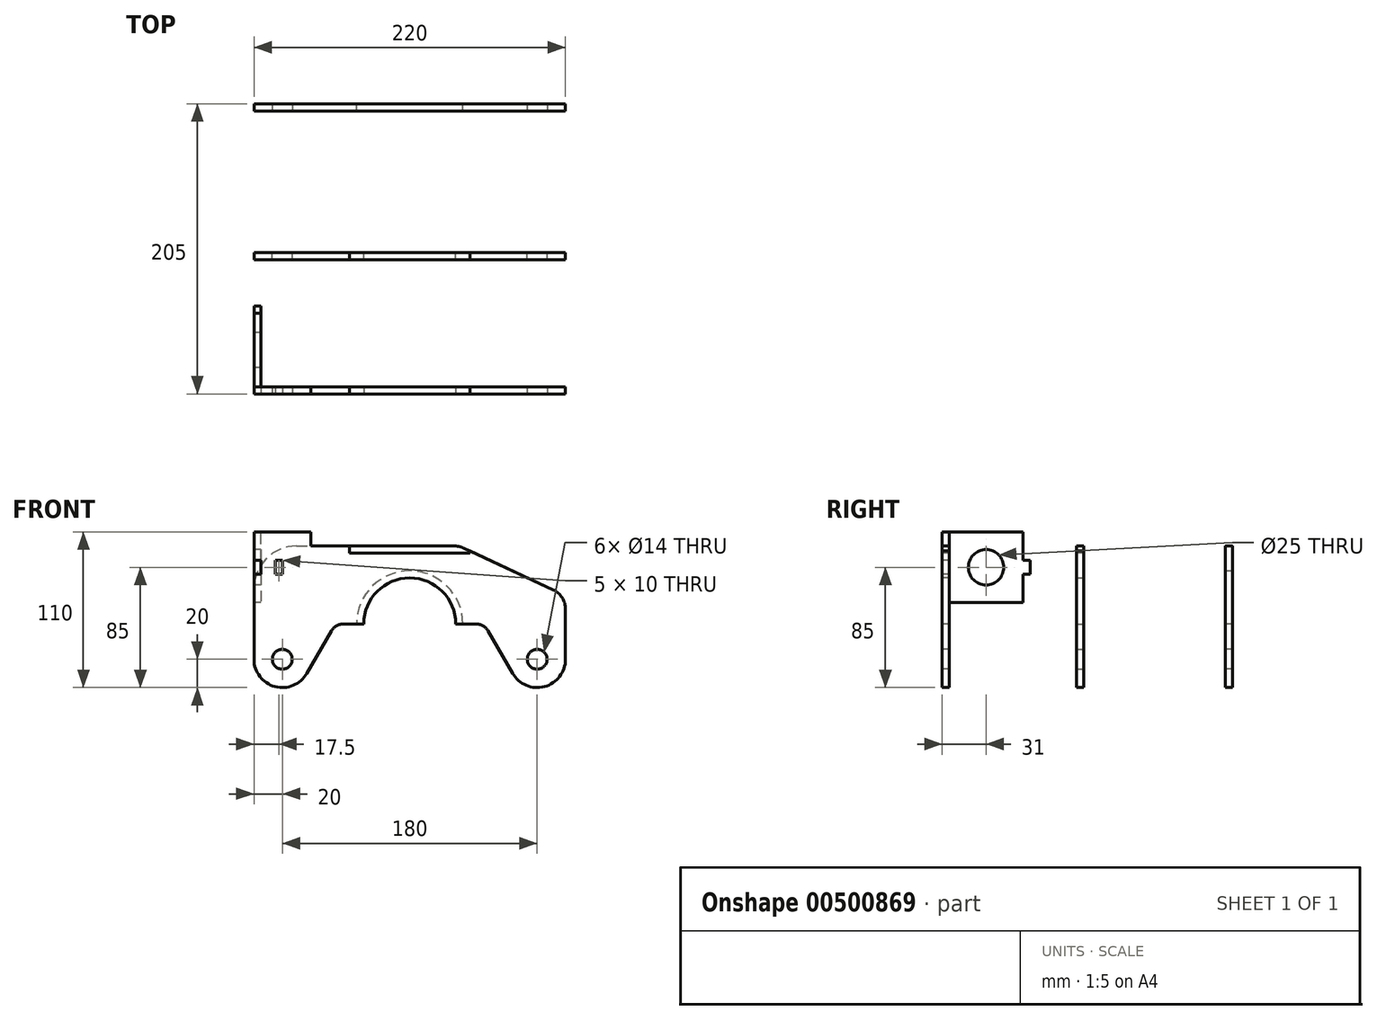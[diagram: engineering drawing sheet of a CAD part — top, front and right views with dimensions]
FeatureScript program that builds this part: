
annotation { "Feature Type Name" : "Feature", "Feature Type Description" : "" }
export const myFeature = defineFeature(function(context is Context, id is Id, definition is map)
    precondition{}
    {
        {
            var Q0;
            Q0=qCreatedBy(makeId("Front.planeOp"),FACE);
            var sketch = newSketch(context, id + "F0", { "sketchPlane" : qUnion([Q0])});
            skArc(sketch, "E0", {"start": v(32.5, 0) * mm, "mid": v(0, 32.5) * mm, "end": v(-32.5, 0) * mm});
            skLineSegment(sketch, "E1", {"start": v(-32.5, 0) * mm, "end": v(32.5, 0) * mm, "construction": true});
            skPoint(sketch, "E2", {"position": v(-90, -25) * mm});
            skCircle(sketch, "E3", {"center": v(-90, -25) * mm, "radius": 7 * mm});
            skCircle(sketch, "E4", {"center": v(-90, -25) * mm, "radius": 20 * mm});
            skPoint(sketch, "E5", {"position": v(90, -25) * mm});
            skCircle(sketch, "E6", {"center": v(90, -25) * mm, "radius": 7 * mm});
            skCircle(sketch, "E7", {"center": v(90, -25) * mm, "radius": 20 * mm});
            skPoint(sketch, "E8", {"position": v(-110, -25) * mm});
            skPoint(sketch, "E9", {"position": v(110, -25) * mm});
            skLineSegment(sketch, "E10", {"start": v(-110, -25) * mm, "end": v(-110, 25) * mm});
            skLineSegment(sketch, "E11", {"start": v(-80, 55) * mm, "end": v(110, 55) * mm});
            skLineSegment(sketch, "E12", {"start": v(110, 55) * mm, "end": v(110, -25) * mm});
            skLineSegment(sketch, "E13", {"start": v(-32.5, 0) * mm, "end": v(-46.72, 0) * mm});
            skLineSegment(sketch, "E14", {"start": v(32.5, 0) * mm, "end": v(46.72, 0) * mm});
            skLineSegment(sketch, "E15", {"start": v(-55.39, -5) * mm, "end": v(-72.67, -34.99) * mm});
            skLineSegment(sketch, "E16", {"start": v(55.39, -5) * mm, "end": v(72.67, -34.99) * mm});
            skPoint(sketch, "E17.visualSharp", {"position": v(-52.5, 0) * mm});
            skArc(sketch, "E17.filletArc", {"start": v(-46.72, 0) * mm, "mid": v(-51.73, -1.34) * mm, "end": v(-55.39, -5) * mm});
            skPoint(sketch, "E18.visualSharp", {"position": v(52.5, 0) * mm});
            skArc(sketch, "E18.filletArc", {"start": v(55.39, -5) * mm, "mid": v(51.73, -1.34) * mm, "end": v(46.72, 0) * mm});
            skPoint(sketch, "E19.visualSharp", {"position": v(-110, 55) * mm});
            skArc(sketch, "E19.filletArc", {"start": v(-80, 55) * mm, "mid": v(-101.21, 46.21) * mm, "end": v(-110, 25) * mm});
            skPoint(sketch, "E20.visualSharp", {"position": v(110, 55) * mm});
            skLineSegment(sketch, "E20.filletArc", {"start": v(110, 55) * mm, "end": v(110, 55) * mm});
            skPoint(sketch, "E21", {"position": v(110, 20) * mm});
            skPoint(sketch, "E22", {"position": v(35, 55) * mm});
            skLineSegment(sketch, "E23", {"start": v(35, 55) * mm, "end": v(110, 20) * mm});
            skSolve(sketch);
        }
        {
            var Q0;
            Q0=makeQuery(id+"F0.imprint","IMPRINT",FACE,{"disambiguationData":[TD([[makeQuery(id+"F0.imprint","IMPRINT",EDGE,{"derivedFrom":sQuery(id+"F0.wireOp",EDGE,"E3")}),-1.0]])]});
            var Q1;
            Q1=makeQuery(id+"F0.imprint","IMPRINT",FACE,{"disambiguationData":[TD([[makeQuery(id+"F0.imprint","IMPRINT",EDGE,{"derivedFrom":sQuery(id+"F0.wireOp",EDGE,"E6")}),-1.0]])]});
            var Q2;
            Q2=makeQuery(id+"F0.imprint","IMPRINT",FACE,{"disambiguationData":[TD([[makeQuery(id+"F0.imprint","IMPRINT",EDGE,{"derivedFrom":sQuery(id+"F0.wireOp",EDGE,"E0")}),-1.0]])]});
            extrude(context, id + "F1", {"entities" : qUnion([Q0, Q1, Q2]), "depth" : 5 * mm, "offsetDistance" : 25 * mm});
        }
        {
            var Q0;
            Q0=qCreatedBy(makeId("Front.planeOp"),FACE);
            cPlane(context, id + "F2", {"entities" : qUnion([Q0]), "cplaneType" : CPlaneType.OFFSET, "offset" : 50 * mm, "oppositeDirection" : true, "width" : 150 * mm, "height" : 150 * mm});
        }
        {
            var Q0;
            Q0=makeQuery(id+"F1.opExtrude","SWEPT_BODY",BODY,{"disambiguationData":[OSD([sQuery(id+"F0.wireOp",EDGE,"E0"),sQuery(id+"F0.wireOp",EDGE,"wYGwPTdj-hQ3h-UPXI-DBvO-CMdxX0ZBpIs3"),sQuery(id+"F0.wireOp",EDGE,"x7k1yNY0-FdVM-nHSz-DSX0-2XPxu6rrP0qx"),sQuery(id+"F0.wireOp",EDGE,"9FEWUdX1-vxY7-CqPM-wlNF-PPAwq3WJZH4g"),sQuery(id+"F0.wireOp",EDGE,"gDaBEeFt-Z0H3-VczB-V8Bx-S3RSHxuVBjjS"),sQuery(id+"F0.wireOp",EDGE,"murKOrwq-gOHJ-bXzC-ZGz9-tcrJ8arLhTBh"),sQuery(id+"F0.wireOp",EDGE,"XS1oxogV-xBYE-ZJ7y-Qyi2-3TEannQxHCB3"),sQuery(id+"F0.wireOp",EDGE,"UnKacQbt-6CPZ-4kxL-4eNt-IC4GjbSk1ORf"),sQuery(id+"F0.wireOp",EDGE,"afb97e3d-8f33-4936-9a61-d90580ab6d3b.filletArc"),sQuery(id+"F0.wireOp",EDGE,"c8fba1ef-1978-42b1-8804-f232b3c369ea.filletArc"),sQuery(id+"F0.wireOp",EDGE,"X5k6Ah4p-kY58-pmaY-KI1E-PuHpooEfadsh"),sQuery(id+"F0.wireOp",EDGE,"EwHy3WlO-al0v-v5lV-Htfk-dZK2AdyTbM4l"),sQuery(id+"F0.wireOp",EDGE,"sK6yQUJL-bbSg-vOET-FAIG-DtKAZYSsNfgG"),sQuery(id+"F0.wireOp",EDGE,"gzghe2TM-HSCt-wxjk-NPDM-RHRqv8zNIVQs"),sQuery(id+"F0.wireOp",EDGE,"0c25a0b1-6eda-4544-9dcf-9f9016e37f78.filletArc"),sQuery(id+"F0.wireOp",EDGE,"3fe3a689-dd35-411c-a34f-f7a2c4317feb.filletArc")])]});
            var Q1;
            Q1=qCreatedBy(id+"F2.planeOp",FACE);
            mirror(context, id + "F3", {"entities" : qUnion([Q0]), "mirrorPlane" : qUnion([Q1])});
        }
        {
            var Q0;
            Q0=makeQuery(id+"F3.opPattern","COPY",FACE,{"derivedFrom":makeQuery(id+"F1.opExtrude","CAP_FACE",FACE,{"disambiguationData":[OSD([sQuery(id+"F0.wireOp",EDGE,"E0"),sQuery(id+"F0.wireOp",EDGE,"wYGwPTdj-hQ3h-UPXI-DBvO-CMdxX0ZBpIs3"),sQuery(id+"F0.wireOp",EDGE,"x7k1yNY0-FdVM-nHSz-DSX0-2XPxu6rrP0qx"),sQuery(id+"F0.wireOp",EDGE,"9FEWUdX1-vxY7-CqPM-wlNF-PPAwq3WJZH4g"),sQuery(id+"F0.wireOp",EDGE,"gDaBEeFt-Z0H3-VczB-V8Bx-S3RSHxuVBjjS"),sQuery(id+"F0.wireOp",EDGE,"murKOrwq-gOHJ-bXzC-ZGz9-tcrJ8arLhTBh"),sQuery(id+"F0.wireOp",EDGE,"XS1oxogV-xBYE-ZJ7y-Qyi2-3TEannQxHCB3"),sQuery(id+"F0.wireOp",EDGE,"UnKacQbt-6CPZ-4kxL-4eNt-IC4GjbSk1ORf"),sQuery(id+"F0.wireOp",EDGE,"afb97e3d-8f33-4936-9a61-d90580ab6d3b.filletArc"),sQuery(id+"F0.wireOp",EDGE,"c8fba1ef-1978-42b1-8804-f232b3c369ea.filletArc"),sQuery(id+"F0.wireOp",EDGE,"X5k6Ah4p-kY58-pmaY-KI1E-PuHpooEfadsh"),sQuery(id+"F0.wireOp",EDGE,"EwHy3WlO-al0v-v5lV-Htfk-dZK2AdyTbM4l"),sQuery(id+"F0.wireOp",EDGE,"sK6yQUJL-bbSg-vOET-FAIG-DtKAZYSsNfgG"),sQuery(id+"F0.wireOp",EDGE,"gzghe2TM-HSCt-wxjk-NPDM-RHRqv8zNIVQs"),sQuery(id+"F0.wireOp",EDGE,"0c25a0b1-6eda-4544-9dcf-9f9016e37f78.filletArc"),sQuery(id+"F0.wireOp",EDGE,"3fe3a689-dd35-411c-a34f-f7a2c4317feb.filletArc")])],"isStart":false}),"instanceName":"1"});
            var sketch = newSketch(context, id + "F4", { "sketchPlane" : qUnion([Q0])});
            skLineSegment(sketch, "E24.0", {"start": v(-32.5, 0) * mm, "end": v(-32.5, 0) * mm});
            skCircle(sketch, "E25", {"center": v(0, 0) * mm, "radius": 37.5 * mm});
            skLineSegment(sketch, "E26", {"start": v(0, 0) * mm, "end": v(37.5, 0) * mm});
            skSolve(sketch);
        }
        {
            var Q0;
            Q0 = qSketchRegion(id + "F4", true);
            extrude(context, id + "F5", {"entities" : qUnion([Q0]), "operationType" : NewBodyOperationType.REMOVE, "oppositeDirection" : true, "depth" : 25 * mm, "offsetDistance" : 25 * mm});
        }
        {
            var Q0;
            Q0=qCreatedBy(makeId("Front.planeOp"),FACE);
            cPlane(context, id + "F6", {"entities" : qUnion([Q0]), "cplaneType" : CPlaneType.OFFSET, "offset" : 50 * mm, "width" : 150 * mm, "height" : 150 * mm});
        }
        {
            var Q0;
            Q0=makeQuery(id+"F1.opExtrude","SWEPT_BODY",BODY,{"disambiguationData":[OSD([sQuery(id+"F0.wireOp",EDGE,"E0"),sQuery(id+"F0.wireOp",EDGE,"wYGwPTdj-hQ3h-UPXI-DBvO-CMdxX0ZBpIs3"),sQuery(id+"F0.wireOp",EDGE,"x7k1yNY0-FdVM-nHSz-DSX0-2XPxu6rrP0qx"),sQuery(id+"F0.wireOp",EDGE,"9FEWUdX1-vxY7-CqPM-wlNF-PPAwq3WJZH4g"),sQuery(id+"F0.wireOp",EDGE,"gDaBEeFt-Z0H3-VczB-V8Bx-S3RSHxuVBjjS"),sQuery(id+"F0.wireOp",EDGE,"murKOrwq-gOHJ-bXzC-ZGz9-tcrJ8arLhTBh"),sQuery(id+"F0.wireOp",EDGE,"XS1oxogV-xBYE-ZJ7y-Qyi2-3TEannQxHCB3"),sQuery(id+"F0.wireOp",EDGE,"UnKacQbt-6CPZ-4kxL-4eNt-IC4GjbSk1ORf"),sQuery(id+"F0.wireOp",EDGE,"afb97e3d-8f33-4936-9a61-d90580ab6d3b.filletArc"),sQuery(id+"F0.wireOp",EDGE,"c8fba1ef-1978-42b1-8804-f232b3c369ea.filletArc"),sQuery(id+"F0.wireOp",EDGE,"X5k6Ah4p-kY58-pmaY-KI1E-PuHpooEfadsh"),sQuery(id+"F0.wireOp",EDGE,"EwHy3WlO-al0v-v5lV-Htfk-dZK2AdyTbM4l"),sQuery(id+"F0.wireOp",EDGE,"sK6yQUJL-bbSg-vOET-FAIG-DtKAZYSsNfgG"),sQuery(id+"F0.wireOp",EDGE,"gzghe2TM-HSCt-wxjk-NPDM-RHRqv8zNIVQs"),sQuery(id+"F0.wireOp",EDGE,"0c25a0b1-6eda-4544-9dcf-9f9016e37f78.filletArc"),sQuery(id+"F0.wireOp",EDGE,"3fe3a689-dd35-411c-a34f-f7a2c4317feb.filletArc")])]});
            var Q1;
            Q1=qCreatedBy(id+"F6.planeOp",FACE);
            mirror(context, id + "F7", {"entities" : qUnion([Q0]), "mirrorPlane" : qUnion([Q1])});
        }
        {
            var Q0;
            Q0=makeQuery(id+"F7.opPattern","COPY",FACE,{"derivedFrom":makeQuery(id+"F1.opExtrude","CAP_FACE",FACE,{"disambiguationData":[OSD([sQuery(id+"F0.wireOp",EDGE,"E0"),sQuery(id+"F0.wireOp",EDGE,"E3"),sQuery(id+"F0.wireOp",EDGE,"E4"),sQuery(id+"F0.wireOp",EDGE,"E6"),sQuery(id+"F0.wireOp",EDGE,"E7"),sQuery(id+"F0.wireOp",EDGE,"E10"),sQuery(id+"F0.wireOp",EDGE,"E11"),sQuery(id+"F0.wireOp",EDGE,"E12"),sQuery(id+"F0.wireOp",EDGE,"E13"),sQuery(id+"F0.wireOp",EDGE,"E14"),sQuery(id+"F0.wireOp",EDGE,"E15"),sQuery(id+"F0.wireOp",EDGE,"E16"),sQuery(id+"F0.wireOp",EDGE,"E17.filletArc"),sQuery(id+"F0.wireOp",EDGE,"E18.filletArc"),sQuery(id+"F0.wireOp",EDGE,"E19.filletArc"),sQuery(id+"F0.wireOp",EDGE,"E20.filletArc")])],"isStart":true}),"instanceName":"1"});
            var sketch = newSketch(context, id + "F8", { "sketchPlane" : qUnion([Q0])});
            skLineSegment(sketch, "E27.0", {"start": v(-110, -25) * mm, "end": v(-110, 25) * mm});
            skLineSegment(sketch, "E28.0", {"start": v(-80, 55) * mm, "end": v(-80, 55) * mm});
            skLineSegment(sketch, "E29", {"start": v(-110, 55) * mm, "end": v(-110, 65) * mm});
            skLineSegment(sketch, "E30", {"start": v(-110, 55) * mm, "end": v(-110, 25) * mm});
            skLineSegment(sketch, "E31", {"start": v(-110, 65) * mm, "end": v(-70, 65) * mm});
            skLineSegment(sketch, "E32", {"start": v(-70, 65) * mm, "end": v(-70, 55) * mm});
            skPoint(sketch, "E33", {"position": v(-110, 45) * mm});
            skLineSegment(sketch, "E34.bottom", {"start": v(-110, 45) * mm, "end": v(-105, 45) * mm});
            skLineSegment(sketch, "E34.top", {"start": v(-110, 35) * mm, "end": v(-105, 35) * mm});
            skLineSegment(sketch, "E34.left", {"start": v(-110, 45) * mm, "end": v(-110, 35) * mm});
            skLineSegment(sketch, "E34.right", {"start": v(-105, 45) * mm, "end": v(-105, 35) * mm});
            skLineSegment(sketch, "E35.bottom", {"start": v(-95, 45) * mm, "end": v(-90, 45) * mm});
            skLineSegment(sketch, "E35.top", {"start": v(-95, 35) * mm, "end": v(-90, 35) * mm});
            skLineSegment(sketch, "E35.left", {"start": v(-95, 45) * mm, "end": v(-95, 35) * mm});
            skLineSegment(sketch, "E35.right", {"start": v(-90, 45) * mm, "end": v(-90, 35) * mm});
            skArc(sketch, "E36.0", {"start": v(-80, 55) * mm, "mid": v(-101.21, 46.21) * mm, "end": v(-110, 25) * mm});
            skSolve(sketch);
        }
        {
            var Q0;
            {var subQ1=sQuery(id+"F8.wireOp",EDGE,"E29");Q0=makeQuery(id+"F8.imprint","IMPRINT",FACE,{"disambiguationData":[TD([[makeQuery(id+"F8.imprint","IMPRINT",EDGE,{"derivedFrom":subQ1}),-1.0]])]});}
            var Q1;
            {var subQ1=sQuery(id+"F8.wireOp",EDGE,"E34.bottom");Q1=makeQuery(id+"F8.imprint","IMPRINT",FACE,{"disambiguationData":[TD([[makeQuery(id+"F8.imprint","IMPRINT",EDGE,{"derivedFrom":subQ1}),-1.0]])]});}
            var Q2;
            {var subQ0=sQuery(id+"F8.wireOp",EDGE,"E36.0");var subQ3=sQuery(id+"F8.wireOp",EDGE,"E34.top");var subQ5=makeQuery(id+"F8.imprint","INTERSECT",VERTEX,{"derivedFrom":[subQ3,subQ0]});Q2=makeQuery(id+"F8.imprint","IMPRINT",FACE,{"disambiguationData":[TD([[makeQuery(id+"F8.imprint","IMPRINT",EDGE,{"disambiguationData":[TD([[subQ5,1.0]])],"derivedFrom":subQ3}),-1.0]])]});}
            extrude(context, id + "F9", {"entities" : qUnion([Q0, Q1, Q2]), "operationType" : NewBodyOperationType.ADD, "oppositeDirection" : true, "depth" : 5 * mm, "offsetDistance" : 25 * mm});
        }
        {
            var Q0;
            Q0=makeQuery(id+"F8.imprint","IMPRINT",FACE,{"disambiguationData":[TD([[makeQuery(id+"F8.imprint","IMPRINT",EDGE,{"derivedFrom":sQuery(id+"F8.wireOp",EDGE,"E35.bottom")}),-1.0]])]});
            var Q1;
            {var subQ1=sQuery(id+"F8.wireOp",EDGE,"E34.bottom");Q1=makeQuery(id+"F8.imprint","IMPRINT",FACE,{"disambiguationData":[TD([[makeQuery(id+"F8.imprint","IMPRINT",EDGE,{"derivedFrom":subQ1}),-1.0]])]});}
            var Q2;
            {var subQ0=sQuery(id+"F8.wireOp",EDGE,"E34.right");var subQ1=sQuery(id+"F8.wireOp",EDGE,"E34.top");var subQ2=makeQuery(id+"F8.imprint","INTERSECT",VERTEX,{"derivedFrom":[subQ1,subQ0]});Q2=makeQuery(id+"F8.imprint","IMPRINT",FACE,{"disambiguationData":[TD([[makeQuery(id+"F8.imprint","IMPRINT",EDGE,{"disambiguationData":[TD([[subQ2,1.0]])],"derivedFrom":subQ1}),1.0]])]});}
            extrude(context, id + "F10", {"entities" : qUnion([Q0, Q1, Q2]), "operationType" : NewBodyOperationType.REMOVE, "oppositeDirection" : true, "depth" : 25 * mm, "offsetDistance" : 25 * mm});
        }
        {
            var Q0;
            Q0=makeQuery(id+"F7.opPattern","COPY",EDGE,{"derivedFrom":makeQuery(id+"F1.opExtrude","SWEPT_EDGE",EDGE,{"disambiguationData":[OSD([sQuery(id+"F0.wireOp",EDGE,"E11"),sQuery(id+"F0.wireOp",EDGE,"E23")])]}),"instanceName":"1"});
            var Q1;
            Q1=makeQuery(id+"F1.opExtrude","SWEPT_EDGE",EDGE,{"disambiguationData":[OSD([sQuery(id+"F0.wireOp",EDGE,"E11"),sQuery(id+"F0.wireOp",EDGE,"E23")])]});
            var Q2;
            Q2=makeQuery(id+"F3.opPattern","COPY",EDGE,{"derivedFrom":makeQuery(id+"F1.opExtrude","SWEPT_EDGE",EDGE,{"disambiguationData":[OSD([sQuery(id+"F0.wireOp",EDGE,"E11"),sQuery(id+"F0.wireOp",EDGE,"E23")])]}),"instanceName":"1"});
            var Q3;
            Q3=makeQuery(id+"F3.opPattern","COPY",EDGE,{"derivedFrom":makeQuery(id+"F1.opExtrude","SWEPT_EDGE",EDGE,{"disambiguationData":[OSD([sQuery(id+"F0.wireOp",EDGE,"E12"),sQuery(id+"F0.wireOp",EDGE,"E23")])]}),"instanceName":"1"});
            var Q4;
            Q4=makeQuery(id+"F7.opPattern","COPY",EDGE,{"derivedFrom":makeQuery(id+"F1.opExtrude","SWEPT_EDGE",EDGE,{"disambiguationData":[OSD([sQuery(id+"F0.wireOp",EDGE,"E12"),sQuery(id+"F0.wireOp",EDGE,"E23")])]}),"instanceName":"1"});
            var Q5;
            Q5=makeQuery(id+"F1.opExtrude","SWEPT_EDGE",EDGE,{"disambiguationData":[OSD([sQuery(id+"F0.wireOp",EDGE,"E12"),sQuery(id+"F0.wireOp",EDGE,"E23")])]});
            fillet(context, id + "F11", {"entities" : qUnion([Q0, Q1, Q2, Q3, Q4, Q5]), "radius" : 15 * mm, "tangentPropagation" : true, "allowEdgeOverflow" : false});
        }
        {
            var Q0;
            {var subQ0=sQuery(id+"F0.wireOp",EDGE,"E11");Q0=makeQuery(id+"F9.boolean.opBoolean","MERGE",FACE,{"derivedFrom":[makeQuery(id+"F7.opPattern","COPY",FACE,{"derivedFrom":makeQuery(id+"F1.opExtrude","CAP_FACE",FACE,{"disambiguationData":[OSD([sQuery(id+"F0.wireOp",EDGE,"E0"),sQuery(id+"F0.wireOp",EDGE,"E3"),sQuery(id+"F0.wireOp",EDGE,"E4"),sQuery(id+"F0.wireOp",EDGE,"E6"),sQuery(id+"F0.wireOp",EDGE,"E7"),sQuery(id+"F0.wireOp",EDGE,"E10"),subQ0,sQuery(id+"F0.wireOp",EDGE,"E12"),sQuery(id+"F0.wireOp",EDGE,"E13"),sQuery(id+"F0.wireOp",EDGE,"E14"),sQuery(id+"F0.wireOp",EDGE,"E15"),sQuery(id+"F0.wireOp",EDGE,"E16"),sQuery(id+"F0.wireOp",EDGE,"E17.filletArc"),sQuery(id+"F0.wireOp",EDGE,"E18.filletArc"),sQuery(id+"F0.wireOp",EDGE,"E19.filletArc"),sQuery(id+"F0.wireOp",EDGE,"E23")])],"isStart":true}),"instanceName":"1"}),makeQuery(id+"F9.opExtrude","CAP_FACE",FACE,{"disambiguationData":[OSD([subQ0,sQuery(id+"F8.wireOp",EDGE,"E29"),sQuery(id+"F8.wireOp",EDGE,"E30"),sQuery(id+"F8.wireOp",EDGE,"E31"),sQuery(id+"F8.wireOp",EDGE,"E32"),sQuery(id+"F8.wireOp",EDGE,"E34.left"),sQuery(id+"F8.wireOp",EDGE,"E36.0")])],"isStart":true})]});}
            var sketch = newSketch(context, id + "F12", { "sketchPlane" : qUnion([Q0])});
            skPoint(sketch, "E37", {"position": v(0, 55) * mm});
            skLineSegment(sketch, "E38", {"start": v(-42.5, 55) * mm, "end": v(-42.5, 50) * mm});
            skLineSegment(sketch, "E39", {"start": v(-42.5, 50) * mm, "end": v(42.5, 50) * mm});
            skLineSegment(sketch, "E40", {"start": v(42.5, 50) * mm, "end": v(42.5, 51.5) * mm});
            skArc(sketch, "E41.0", {"start": v(38.02, 53.6) * mm, "mid": v(34.92, 54.64) * mm, "end": v(31.67, 55) * mm});
            skLineSegment(sketch, "E42", {"start": v(38.02, 53.6) * mm, "end": v(42.5, 51.5) * mm});
            skLineSegment(sketch, "E43", {"start": v(-42.5, 55) * mm, "end": v(-70, 65) * mm});
            skLineSegment(sketch, "E44", {"start": v(-70, 65) * mm, "end": v(31.67, 55) * mm});
            skSolve(sketch);
        }
        {
            var Q0;
            Q0 = qSketchRegion(id + "F12", true);
            extrude(context, id + "F13", {"entities" : qUnion([Q0]), "operationType" : NewBodyOperationType.REMOVE, "oppositeDirection" : true, "depth" : 100 * mm, "offsetDistance" : 25 * mm});
        }
        {
            var Q0;
            {var subQ1=sQuery(id+"F8.wireOp",EDGE,"E34.left");var subQ3=sQuery(id+"F8.wireOp",EDGE,"E31");var subQ4=sQuery(id+"F8.wireOp",EDGE,"E30");var subQ5=sQuery(id+"F8.wireOp",EDGE,"E29");var subQ16=sQuery(id+"F0.wireOp",EDGE,"E10");Q0=makeQuery(id+"F10.boolean.opBoolean","SPLIT",FACE,{"disambiguationData":[TD([makeQuery(id+"F9.opExtrude","SWEPT_FACE",FACE,{"disambiguationData":[OSD([subQ3])]})])],"derivedFrom":makeQuery(id+"F9.boolean.opBoolean","MERGE",FACE,{"derivedFrom":[makeQuery(id+"F7.opPattern","COPY",FACE,{"derivedFrom":makeQuery(id+"F1.opExtrude","SWEPT_FACE",FACE,{"disambiguationData":[OSD([subQ16])]}),"instanceName":"1"}),makeQuery(id+"F9.opExtrude","SWEPT_FACE",FACE,{"disambiguationData":[OSD([subQ5,subQ4,subQ1])]})]})});}
            var sketch = newSketch(context, id + "F14", { "sketchPlane" : qUnion([Q0])});
            skLineSegment(sketch, "E45.0", {"start": v(95, 45) * mm, "end": v(100, 45) * mm});
            skLineSegment(sketch, "E46.0", {"start": v(100, 45) * mm, "end": v(100, 35) * mm});
            skLineSegment(sketch, "E47.0", {"start": v(95, 35) * mm, "end": v(100, 35) * mm});
            skLineSegment(sketch, "E48", {"start": v(95, 45) * mm, "end": v(95, 65) * mm});
            skLineSegment(sketch, "E49", {"start": v(95, 65) * mm, "end": v(43, 65) * mm});
            skLineSegment(sketch, "E50", {"start": v(95, 35) * mm, "end": v(95, 15) * mm});
            skLineSegment(sketch, "E51", {"start": v(95, 15) * mm, "end": v(43, 15) * mm});
            skLineSegment(sketch, "E52", {"start": v(69, 65) * mm, "end": v(69, 15) * mm, "construction": true});
            skLineSegment(sketch, "E53.MirrorCS", {"start": v(43, 35) * mm, "end": v(43, 15) * mm});
            skLineSegment(sketch, "E54.MirrorCS", {"start": v(43, 35) * mm, "end": v(38, 35) * mm});
            skLineSegment(sketch, "E55.MirrorCS", {"start": v(38, 45) * mm, "end": v(38, 35) * mm});
            skLineSegment(sketch, "E56.MirrorCS", {"start": v(43, 45) * mm, "end": v(43, 65) * mm});
            skLineSegment(sketch, "E57.MirrorCS", {"start": v(43, 45) * mm, "end": v(38, 45) * mm});
            skCircle(sketch, "E58", {"center": v(69, 40) * mm, "radius": 12.5 * mm});
            skSolve(sketch);
        }
        {
            var Q0;
            Q0=makeQuery(id+"F14.imprint","IMPRINT",FACE,{"disambiguationData":[TD([[makeQuery(id+"F14.imprint","IMPRINT",EDGE,{"derivedFrom":sQuery(id+"F14.wireOp",EDGE,"E45.0")}),-1.0]])]});
            extrude(context, id + "F15", {"entities" : qUnion([Q0]), "oppositeDirection" : true, "depth" : 5 * mm, "offsetDistance" : 25 * mm});
        }
    });
